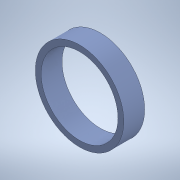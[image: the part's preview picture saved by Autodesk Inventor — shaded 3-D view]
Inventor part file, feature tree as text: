
AUTODESK INVENTOR PART (.ipt)
format: ipt  version: 2020 (Build 240168000, 168)  size: 102,912 bytes
history: native  units: in
note: dims shown in document units (in); Inventor stores cm internally (conversion verified against a paired STEP export)
features: extrude x1, sketch x1
ambient origin geometry x8: Origin, YZ Plane, XZ Plane, XY Plane, X Axis, Y Axis, Z Axis, Center Point
bodies: Solid1 (feature_tree)
feature tree (2):
  extrude  "Extrusion1"  Depth=1.0in TaperAngle=0.0deg
  sketch  "Sketch1"  dims[d0=4.25in d1=1.0in d2=0.0in d3=0.28in]
